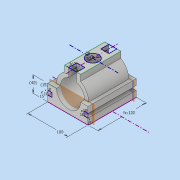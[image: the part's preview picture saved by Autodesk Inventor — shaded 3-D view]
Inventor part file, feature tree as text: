
AUTODESK INVENTOR PART (.ipt)
format: ipt  version: 2019 (Build 230136000, 136)  size: 211,968 bytes
history: native  units: mm
features: other x10, extrude x7, projected_geometry x1
ambient origin geometry x8: Origin, YZ Plane, XZ Plane, XY Plane, X Axis, Y Axis, Z Axis, Center Point
bodies: Body1 (feature_tree)
feature tree (18):
  other  "<userpath>\source\LW2020\lw_2021\LW_SAPR\parametres.xlsx"
  other  "Твердое тело1"
  extrude  "Выдавливание1"  Depth=120.0mm
  other  "tube"
  extrude  "Углубление 1"  Depth=100.0mm
  extrude  "Паз 1"  Depth=40.0mm TaperAngle=0.0deg
  other  "paz2"
  other  "фронт1"
  other  "фронт2"
  extrude  "Выдавливание9"  Depth=120.0mm TaperAngle=0.0deg
  other  "top"
  extrude  "Выдавливание10"  Depth=60.0mm
  extrude  "Выдавливание11"  Depth=10.0mm
  extrude  "Выдавливание12"  Depth=10.0mm
  other  "bottom"
  other  "paz1"
  other  "front_arc"
  projected_geometry  "Спроецированная петля1"
